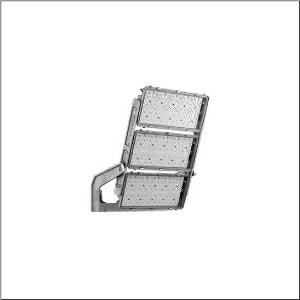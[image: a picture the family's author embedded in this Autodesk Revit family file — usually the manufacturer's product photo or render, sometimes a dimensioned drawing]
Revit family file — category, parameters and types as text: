
# Revit family: floodlight_fl_11_maxi_pro_remote___pl43_5xa779427a01ba_e28e
name_source: partatom
category: Lighting Fixtures
units: mm (PartAtom-declared; Revit-internal decimal feet)

## family parameters
Cut with Voids When Loaded = No
Host = Face
Light Source = No
Part Type = Normal
Room Calculation Point = No
Round Connector Dimension = Use Diameter
Shared = No

## types (1)
- --- (1 x LED, 151320 lm, 1095.9 W, 5000K)
    Apparent Load = 1096 VA
    CIE Flux Codes = 25 74 99 100 100
    Color Rendering = 70
    Color Temperature = 5000K
    Default Elevation = 1800 mm
    Description = Floodlight FL 11  maxi  pro Remote floodlight; light control with lens of PMMA; cover panel of toughened safety glass, transparent; light distribution: PL43, asymmetric direct distribution, LEDcolour temperature: 5000K, rated luminous flux: 151.320lm, colour rendering: CRI > 70, light colour: 750; luminous efficacy: 138lm/W; brightness control: DALI 2 (1 DALI address); with terminal, 8-pole, max. 2.5mm², mains connection: 220..240V/380..400V AC, 50/60Hz, surge voltage resistance: line to ground: 10kV, ECG replaceable separately, no afterglow with DALI off / DMX off command, LED unit replaceable without ESD environment, dustproof LED module, dimming range 10..100%; 1096W floodlight with 2x LED unit of diecast aluminium, coated grey; length: 713mm / width: 651mm / height: 338mm; mounting bracket, of diecast aluminium, uncoated, natural, equipment: Power, protection rating (complete): IP66; insulation class (complete): insulation class I (protective earthing); certification: CE, ENEC, VDE; ball protection: ball impact resistance with accessories, impact resistance: IK07; only for outdoor installations, rated ambient temperature 10°C, permissible operating ambient temperature: -40..+30°C, permissible storage temperature: -40..+85°Cpackaging unit: 1 piece

Light Distribution: PL43
    Height = 320 mm
    Lamp = 1 x LED
    Lamp Light Flux = 151320 lm
    Lamp Power = 1095.9 W
    Lamp count = 1
    Length = 1002 mm
    Luminous efficacy = 138 lm/W
    Manufacturer = Siteco
    ModVariant = No
    Model = 5XA779427A01BA
    Mounting Place = Ceiling
    Mounting Type = Surface mounted
    Number of Poles = 1
    OnlyDefault = Yes
    Power Factor = 1
    Product Name = Floodlight FL 11 maxi pro Remote | PL43
    Product group = floodlight | ceiling mounted
    ProductGroupID = 301
    Protection Class = Protection class I
    Protection Degree = IP 66
    RLX_Detail_Level = 1
    RLX_Emergency_Light_Flux = 0 lm
    RLX_Emergency_Type = 0
    RLX_Emergency_Type_DB = No
    RlxData = <blob elided: 52481 chars, md5=39274f9c>
    Socket = socket
    Standby Power = 0 W
    System Light Flux = 151320 lm
    System Power = 1096 W
    Type Comments = factory setting: luminous flux: 100 % | dim-lin: 254 | 760 mA
    Type Image = l_1349141.jpg
    URL = http://relux.com
    VarID = @adj_096302
    Voltage = 0 V
    Weight = 0.00 kg
    Width = 655 mm

## geometry (parser evidence)
native form markers: Blend x4, Sweep x13
no freeform markers — native parametric forms only
